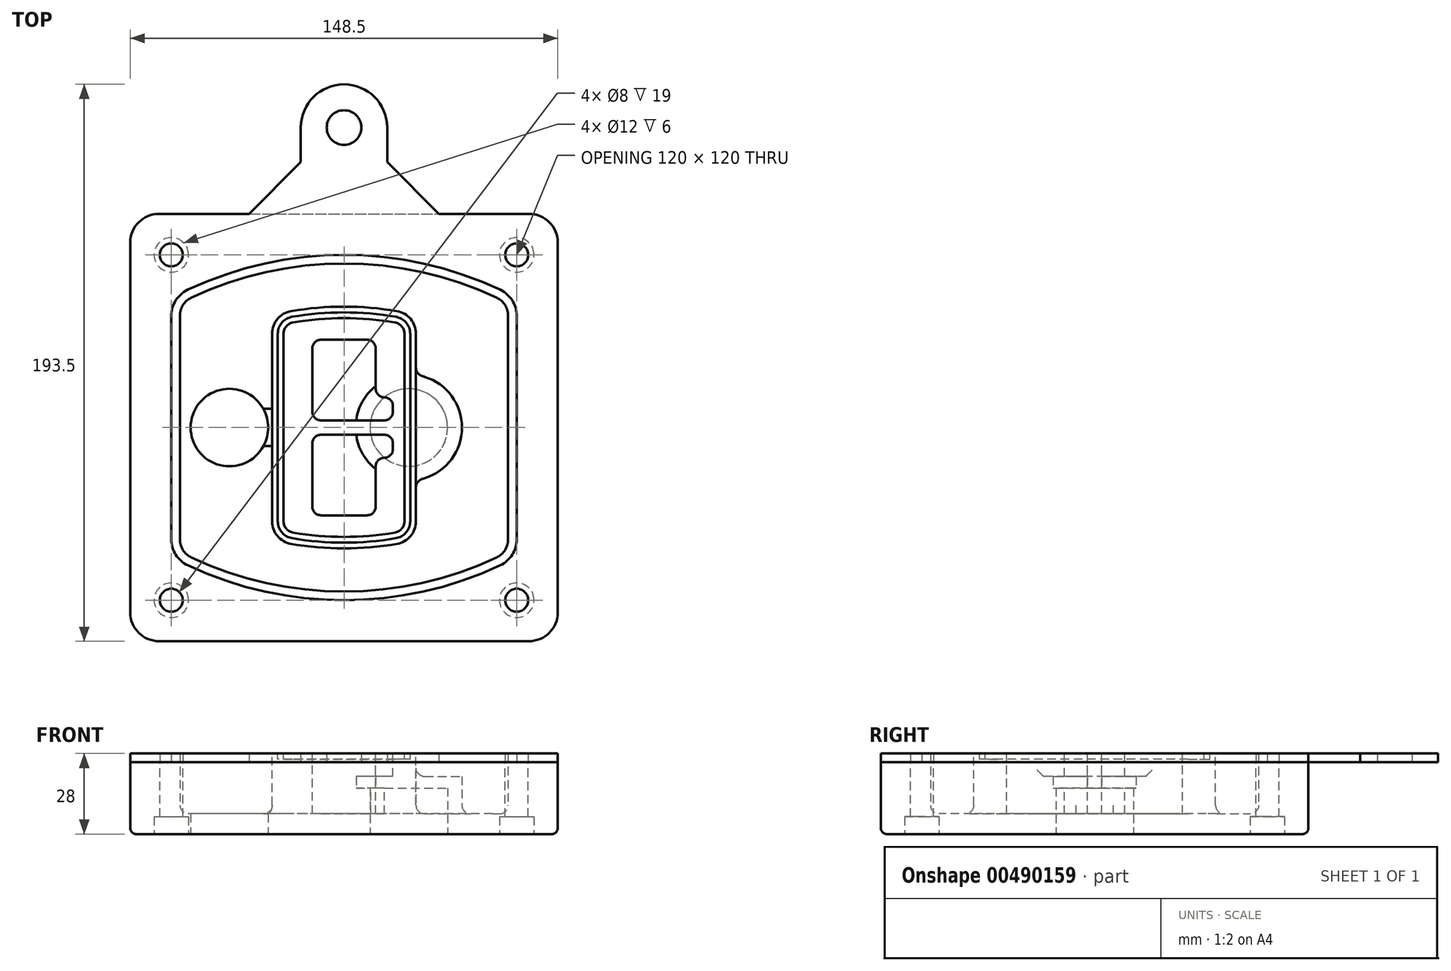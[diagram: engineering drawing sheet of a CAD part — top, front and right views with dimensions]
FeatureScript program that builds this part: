
annotation { "Feature Type Name" : "Feature", "Feature Type Description" : "" }
export const myFeature = defineFeature(function(context is Context, id is Id, definition is map)
    precondition{}
    {
        {
            var Q0;
            Q0=qCreatedBy(makeId("Top.planeOp"),FACE);
            var sketch = newSketch(context, id + "F0", { "sketchPlane" : qUnion([Q0])});
            skPoint(sketch, "E0.rect.middle", {"position": v(0, 0) * mm});
            skLineSegment(sketch, "E1.bottom", {"start": v(-64.25, -74.25) * mm, "end": v(64.25, -74.25) * mm});
            skLineSegment(sketch, "E1.top", {"start": v(-64.25, 74.25) * mm, "end": v(64.25, 74.25) * mm});
            skLineSegment(sketch, "E1.left", {"start": v(-74.25, -64.25) * mm, "end": v(-74.25, 64.25) * mm});
            skLineSegment(sketch, "E1.right", {"start": v(74.25, -64.25) * mm, "end": v(74.25, 64.25) * mm});
            skLineSegment(sketch, "E2", {"start": v(-74.25, 74.25) * mm, "end": v(74.25, -74.25) * mm, "construction": true});
            skLineSegment(sketch, "E3", {"start": v(74.25, 74.25) * mm, "end": v(-74.25, -74.25) * mm, "construction": true});
            skCircle(sketch, "E4", {"center": v(-60, 60) * mm, "radius": 4 * mm});
            skCircle(sketch, "E5", {"center": v(60, 60) * mm, "radius": 4 * mm});
            skCircle(sketch, "E6", {"center": v(60, -60) * mm, "radius": 4 * mm});
            skCircle(sketch, "E7", {"center": v(-60, -60) * mm, "radius": 4 * mm});
            skLineSegment(sketch, "E8", {"start": v(-60, 60) * mm, "end": v(60, 60) * mm, "construction": true});
            skLineSegment(sketch, "E9", {"start": v(60, 60) * mm, "end": v(60, -60) * mm, "construction": true});
            skLineSegment(sketch, "E10", {"start": v(60, -60) * mm, "end": v(-60, -60) * mm, "construction": true});
            skLineSegment(sketch, "E11", {"start": v(-60, -60) * mm, "end": v(-60, 60) * mm, "construction": true});
            skLineSegment(sketch, "E12", {"start": v(-60, 38.83) * mm, "end": v(-60, -38.83) * mm});
            skLineSegment(sketch, "E13", {"start": v(60, 38.83) * mm, "end": v(60, -38.83) * mm});
            skArc(sketch, "E14", {"start": v(54.26, 47.88) * mm, "mid": v(0, 60) * mm, "end": v(-54.26, 47.88) * mm});
            skArc(sketch, "E15", {"start": v(-54.26, -47.88) * mm, "mid": v(0, -60) * mm, "end": v(54.26, -47.88) * mm});
            skLineSegment(sketch, "E16", {"start": v(-60, 0) * mm, "end": v(60, 0) * mm, "construction": true});
            skPoint(sketch, "E17.visualSharp", {"position": v(-60, -45) * mm});
            skArc(sketch, "E17.filletArc", {"start": v(-60, -38.83) * mm, "mid": v(-58.44, -44.2) * mm, "end": v(-54.26, -47.88) * mm});
            skPoint(sketch, "E18.visualSharp", {"position": v(-60, 45) * mm});
            skArc(sketch, "E18.filletArc", {"start": v(-54.26, 47.88) * mm, "mid": v(-58.44, 44.2) * mm, "end": v(-60, 38.83) * mm});
            skPoint(sketch, "E19.visualSharp", {"position": v(60, 45) * mm});
            skArc(sketch, "E19.filletArc", {"start": v(60, 38.83) * mm, "mid": v(58.44, 44.2) * mm, "end": v(54.26, 47.88) * mm});
            skPoint(sketch, "E20.visualSharp", {"position": v(60, -45) * mm});
            skArc(sketch, "E20.filletArc", {"start": v(54.26, -47.88) * mm, "mid": v(58.44, -44.2) * mm, "end": v(60, -38.83) * mm});
            skPoint(sketch, "E21.visualSharp", {"position": v(-74.25, 74.25) * mm});
            skArc(sketch, "E21.filletArc", {"start": v(-64.25, 74.25) * mm, "mid": v(-71.32, 71.32) * mm, "end": v(-74.25, 64.25) * mm});
            skPoint(sketch, "E22.visualSharp", {"position": v(74.25, 74.25) * mm});
            skArc(sketch, "E22.filletArc", {"start": v(74.25, 64.25) * mm, "mid": v(71.32, 71.32) * mm, "end": v(64.25, 74.25) * mm});
            skPoint(sketch, "E23.visualSharp", {"position": v(74.25, -74.25) * mm});
            skArc(sketch, "E23.filletArc", {"start": v(64.25, -74.25) * mm, "mid": v(71.32, -71.32) * mm, "end": v(74.25, -64.25) * mm});
            skPoint(sketch, "E24.visualSharp", {"position": v(-74.25, -74.25) * mm});
            skArc(sketch, "E24.filletArc", {"start": v(-74.25, -64.25) * mm, "mid": v(-71.32, -71.32) * mm, "end": v(-64.25, -74.25) * mm});
            skArc(sketch, "E25.0", {"start": v(57, 38.83) * mm, "mid": v(55.9, 42.58) * mm, "end": v(52.98, 45.17) * mm});
            skLineSegment(sketch, "E25.1", {"start": v(57, 38.83) * mm, "end": v(57, -38.83) * mm});
            skArc(sketch, "E25.2", {"start": v(52.98, -45.17) * mm, "mid": v(55.9, -42.58) * mm, "end": v(57, -38.83) * mm});
            skArc(sketch, "E25.3", {"start": v(-52.98, -45.17) * mm, "mid": v(0, -57) * mm, "end": v(52.98, -45.17) * mm});
            skArc(sketch, "E25.4", {"start": v(-57, -38.83) * mm, "mid": v(-55.9, -42.58) * mm, "end": v(-52.98, -45.17) * mm});
            skArc(sketch, "E25.5", {"start": v(52.98, 45.17) * mm, "mid": v(0, 57) * mm, "end": v(-52.98, 45.17) * mm});
            skLineSegment(sketch, "E25.6", {"start": v(-57, 38.83) * mm, "end": v(-57, -38.83) * mm});
            skArc(sketch, "E25.7", {"start": v(-52.98, 45.17) * mm, "mid": v(-55.9, 42.58) * mm, "end": v(-57, 38.83) * mm});
            skArc(sketch, "E26.0", {"start": v(-55.96, 51.5) * mm, "mid": v(-61.82, 46.33) * mm, "end": v(-64, 38.83) * mm});
            skArc(sketch, "E26.1", {"start": v(55.96, 51.5) * mm, "mid": v(0, 64) * mm, "end": v(-55.96, 51.5) * mm});
            skArc(sketch, "E26.2", {"start": v(64, 38.83) * mm, "mid": v(61.82, 46.33) * mm, "end": v(55.96, 51.5) * mm});
            skLineSegment(sketch, "E26.3", {"start": v(64, 38.83) * mm, "end": v(64, -38.83) * mm});
            skArc(sketch, "E26.4", {"start": v(55.96, -51.5) * mm, "mid": v(61.82, -46.33) * mm, "end": v(64, -38.83) * mm});
            skLineSegment(sketch, "E26.5", {"start": v(-64, 38.83) * mm, "end": v(-64, -38.83) * mm});
            skArc(sketch, "E26.6", {"start": v(-55.96, -51.5) * mm, "mid": v(0, -64) * mm, "end": v(55.96, -51.5) * mm});
            skArc(sketch, "E26.7", {"start": v(-64, -38.83) * mm, "mid": v(-61.82, -46.33) * mm, "end": v(-55.96, -51.5) * mm});
            skSolve(sketch);
        }
        {
            var Q0;
            Q0=makeQuery(id+"F0.imprint","IMPRINT",FACE,{"disambiguationData":[TD([[makeQuery(id+"F0.imprint","IMPRINT",EDGE,{"derivedFrom":sQuery(id+"F0.wireOp",EDGE,"E1.bottom")}),1.0]])]});
            var Q1;
            Q1=makeQuery(id+"F0.imprint","IMPRINT",FACE,{"disambiguationData":[TD([[makeQuery(id+"F0.imprint","IMPRINT",EDGE,{"derivedFrom":sQuery(id+"F0.wireOp",EDGE,"E12")}),1.0]])]});
            var Q2;
            Q2=makeQuery(id+"F0.imprint","IMPRINT",FACE,{"disambiguationData":[TD([[makeQuery(id+"F0.imprint","IMPRINT",EDGE,{"derivedFrom":sQuery(id+"F0.wireOp",EDGE,"E25.0")}),1.0]])]});
            var Q3;
            Q3=makeQuery(id+"F0.imprint","IMPRINT",FACE,{"disambiguationData":[TD([[makeQuery(id+"F0.imprint","IMPRINT",EDGE,{"derivedFrom":sQuery(id+"F0.wireOp",EDGE,"E12")}),-1.0]])]});
            extrude(context, id + "F1", {"entities" : qUnion([Q0, Q1, Q2, Q3]), "oppositeDirection" : true, "depth" : 25 * mm});
        }
        {
            var Q0;
            Q0=makeQuery(id+"F0.imprint","IMPRINT",FACE,{"disambiguationData":[TD([[makeQuery(id+"F0.imprint","IMPRINT",EDGE,{"derivedFrom":sQuery(id+"F0.wireOp",EDGE,"E12")}),1.0]])]});
            extrude(context, id + "F2", {"entities" : qUnion([Q0]), "operationType" : NewBodyOperationType.ADD, "depth" : 3 * mm});
        }
        {
            var Q0;
            Q0=makeQuery(id+"F0.imprint","IMPRINT",FACE,{"disambiguationData":[TD([[makeQuery(id+"F0.imprint","IMPRINT",EDGE,{"derivedFrom":sQuery(id+"F0.wireOp",EDGE,"E25.0")}),1.0]])]});
            extrude(context, id + "F3", {"entities" : qUnion([Q0]), "operationType" : NewBodyOperationType.REMOVE, "oppositeDirection" : true, "depth" : 18 * mm});
        }
        {
            var Q0;
            Q0=makeQuery(id+"F2.opExtrude","CAP_FACE",FACE,{"disambiguationData":[OSD([sQuery(id+"F0.wireOp",EDGE,"E12"),sQuery(id+"F0.wireOp",EDGE,"E13"),sQuery(id+"F0.wireOp",EDGE,"E14"),sQuery(id+"F0.wireOp",EDGE,"E15"),sQuery(id+"F0.wireOp",EDGE,"E17.filletArc"),sQuery(id+"F0.wireOp",EDGE,"E18.filletArc"),sQuery(id+"F0.wireOp",EDGE,"E19.filletArc"),sQuery(id+"F0.wireOp",EDGE,"E20.filletArc"),sQuery(id+"F0.wireOp",EDGE,"E25.0"),sQuery(id+"F0.wireOp",EDGE,"E25.1"),sQuery(id+"F0.wireOp",EDGE,"E25.2"),sQuery(id+"F0.wireOp",EDGE,"E25.3"),sQuery(id+"F0.wireOp",EDGE,"E25.4"),sQuery(id+"F0.wireOp",EDGE,"E25.5"),sQuery(id+"F0.wireOp",EDGE,"E25.6"),sQuery(id+"F0.wireOp",EDGE,"E25.7")])],"isStart":false});
            var sketch = newSketch(context, id + "F4", { "sketchPlane" : qUnion([Q0])});
            skArc(sketch, "E27.0", {"start": v(-18.34, -40.45) * mm, "mid": v(0, -42) * mm, "end": v(18.34, -40.45) * mm});
            skArc(sketch, "E28.0", {"start": v(18.34, 40.45) * mm, "mid": v(0, 42) * mm, "end": v(-18.34, 40.45) * mm});
            skLineSegment(sketch, "E29", {"start": v(-25, 32.57) * mm, "end": v(-25, -32.57) * mm});
            skLineSegment(sketch, "E30", {"start": v(25, 32.57) * mm, "end": v(25, -32.57) * mm});
            skLineSegment(sketch, "E31", {"start": v(-25, 39.1) * mm, "end": v(25, 39.1) * mm, "construction": true});
            skLineSegment(sketch, "E32", {"start": v(-25, -39.1) * mm, "end": v(25, -39.1) * mm, "construction": true});
            skPoint(sketch, "E33.visualSharp", {"position": v(-25, 39.1) * mm});
            skArc(sketch, "E33.filletArc", {"start": v(-18.34, 40.45) * mm, "mid": v(-23.11, 37.73) * mm, "end": v(-25, 32.57) * mm});
            skPoint(sketch, "E34.visualSharp", {"position": v(25, 39.1) * mm});
            skArc(sketch, "E34.filletArc", {"start": v(25, 32.57) * mm, "mid": v(23.11, 37.73) * mm, "end": v(18.34, 40.45) * mm});
            skPoint(sketch, "E35.visualSharp", {"position": v(25, -39.1) * mm});
            skArc(sketch, "E35.filletArc", {"start": v(18.34, -40.45) * mm, "mid": v(23.11, -37.73) * mm, "end": v(25, -32.57) * mm});
            skPoint(sketch, "E36.visualSharp", {"position": v(-25, -39.1) * mm});
            skArc(sketch, "E36.filletArc", {"start": v(-25, -32.57) * mm, "mid": v(-23.11, -37.73) * mm, "end": v(-18.34, -40.45) * mm});
            skArc(sketch, "E37.0", {"start": v(52.98, 45.17) * mm, "mid": v(0, 57) * mm, "end": v(-52.98, 45.17) * mm});
            skArc(sketch, "E37.1", {"start": v(-52.98, 45.17) * mm, "mid": v(-55.9, 42.58) * mm, "end": v(-57, 38.83) * mm});
            skLineSegment(sketch, "E37.2", {"start": v(-57, 38.83) * mm, "end": v(-57, -38.83) * mm});
            skArc(sketch, "E37.3", {"start": v(-57, -38.83) * mm, "mid": v(-55.9, -42.58) * mm, "end": v(-52.98, -45.17) * mm});
            skArc(sketch, "E37.4", {"start": v(-52.98, -45.17) * mm, "mid": v(0, -57) * mm, "end": v(52.98, -45.17) * mm});
            skArc(sketch, "E37.5", {"start": v(52.98, -45.17) * mm, "mid": v(55.9, -42.58) * mm, "end": v(57, -38.83) * mm});
            skLineSegment(sketch, "E37.6", {"start": v(57, 38.83) * mm, "end": v(57, -38.83) * mm});
            skArc(sketch, "E37.7", {"start": v(57, 38.83) * mm, "mid": v(55.9, 42.58) * mm, "end": v(52.98, 45.17) * mm});
            skLineSegment(sketch, "E38.0", {"start": v(23, 32.57) * mm, "end": v(23, -32.57) * mm});
            skArc(sketch, "E38.1", {"start": v(18, -38.48) * mm, "mid": v(21.58, -36.44) * mm, "end": v(23, -32.57) * mm});
            skArc(sketch, "E38.2", {"start": v(-18, -38.48) * mm, "mid": v(0, -40) * mm, "end": v(18, -38.48) * mm});
            skArc(sketch, "E38.3", {"start": v(-23, -32.57) * mm, "mid": v(-21.58, -36.44) * mm, "end": v(-18, -38.48) * mm});
            skLineSegment(sketch, "E38.4", {"start": v(-23, 32.57) * mm, "end": v(-23, -32.57) * mm});
            skArc(sketch, "E38.5", {"start": v(23, 32.57) * mm, "mid": v(21.58, 36.44) * mm, "end": v(18, 38.48) * mm});
            skArc(sketch, "E38.6", {"start": v(-18, 38.48) * mm, "mid": v(-21.58, 36.44) * mm, "end": v(-23, 32.57) * mm});
            skArc(sketch, "E38.7", {"start": v(18, 38.48) * mm, "mid": v(0, 40) * mm, "end": v(-18, 38.48) * mm});
            skArc(sketch, "E39.0", {"start": v(21, 32.57) * mm, "mid": v(20.06, 35.15) * mm, "end": v(17.67, 36.5) * mm});
            skLineSegment(sketch, "E39.1", {"start": v(21, 32.57) * mm, "end": v(21, -32.57) * mm});
            skArc(sketch, "E39.2", {"start": v(17.67, -36.5) * mm, "mid": v(20.06, -35.15) * mm, "end": v(21, -32.57) * mm});
            skArc(sketch, "E39.3", {"start": v(-17.67, -36.5) * mm, "mid": v(0, -38) * mm, "end": v(17.67, -36.5) * mm});
            skArc(sketch, "E39.4", {"start": v(-21, -32.57) * mm, "mid": v(-20.06, -35.15) * mm, "end": v(-17.67, -36.5) * mm});
            skArc(sketch, "E39.5", {"start": v(17.67, 36.5) * mm, "mid": v(0, 38) * mm, "end": v(-17.67, 36.5) * mm});
            skLineSegment(sketch, "E39.6", {"start": v(-21, 32.57) * mm, "end": v(-21, -32.57) * mm});
            skArc(sketch, "E39.7", {"start": v(-17.67, 36.5) * mm, "mid": v(-20.06, 35.15) * mm, "end": v(-21, 32.57) * mm});
            skLineSegment(sketch, "E40", {"start": v(-25, 0) * mm, "end": v(25, 0) * mm, "construction": true});
            skLineSegment(sketch, "E41", {"start": v(-11, 5.5) * mm, "end": v(-11, 27.5) * mm});
            skLineSegment(sketch, "E42", {"start": v(-8, 30.5) * mm, "end": v(8, 30.5) * mm});
            skLineSegment(sketch, "E43", {"start": v(11, 27.5) * mm, "end": v(11, 13.5) * mm});
            skLineSegment(sketch, "E44", {"start": v(14, 10.5) * mm, "end": v(14, 10.5) * mm});
            skLineSegment(sketch, "E45", {"start": v(17, 7.5) * mm, "end": v(17, 5.5) * mm});
            skLineSegment(sketch, "E46", {"start": v(14, 2.5) * mm, "end": v(-8, 2.5) * mm});
            skPoint(sketch, "E47.visualSharp", {"position": v(-11, 30.5) * mm});
            skArc(sketch, "E47.filletArc", {"start": v(-8, 30.5) * mm, "mid": v(-10.12, 29.62) * mm, "end": v(-11, 27.5) * mm});
            skPoint(sketch, "E48.visualSharp", {"position": v(11, 30.5) * mm});
            skArc(sketch, "E48.filletArc", {"start": v(11, 27.5) * mm, "mid": v(10.12, 29.62) * mm, "end": v(8, 30.5) * mm});
            skPoint(sketch, "E49.visualSharp", {"position": v(11, 10.5) * mm});
            skArc(sketch, "E49.filletArc", {"start": v(11, 13.5) * mm, "mid": v(11.88, 11.38) * mm, "end": v(14, 10.5) * mm});
            skPoint(sketch, "E50.visualSharp", {"position": v(17, 10.5) * mm});
            skArc(sketch, "E50.filletArc", {"start": v(17, 7.5) * mm, "mid": v(16.12, 9.62) * mm, "end": v(14, 10.5) * mm});
            skPoint(sketch, "E51.visualSharp", {"position": v(17, 2.5) * mm});
            skArc(sketch, "E51.filletArc", {"start": v(14, 2.5) * mm, "mid": v(16.12, 3.38) * mm, "end": v(17, 5.5) * mm});
            skPoint(sketch, "E52.visualSharp", {"position": v(-11, 2.5) * mm});
            skArc(sketch, "E52.filletArc", {"start": v(-11, 5.5) * mm, "mid": v(-10.12, 3.38) * mm, "end": v(-8, 2.5) * mm});
            skLineSegment(sketch, "E53.0.MirrorCS", {"start": v(14, -2.5) * mm, "end": v(-8, -2.5) * mm});
            skArc(sketch, "E54.0.MirrorCS", {"start": v(-11, -5.5) * mm, "mid": v(-10.12, -3.38) * mm, "end": v(-8, -2.5) * mm});
            skLineSegment(sketch, "E55.0.MirrorCS", {"start": v(-11, -5.5) * mm, "end": v(-11, -27.5) * mm});
            skArc(sketch, "E56.0.MirrorCS", {"start": v(-8, -30.5) * mm, "mid": v(-10.12, -29.62) * mm, "end": v(-11, -27.5) * mm});
            skLineSegment(sketch, "E57.0.MirrorCS", {"start": v(-8, -30.5) * mm, "end": v(8, -30.5) * mm});
            skArc(sketch, "E58.0.MirrorCS", {"start": v(11, -27.5) * mm, "mid": v(10.12, -29.62) * mm, "end": v(8, -30.5) * mm});
            skLineSegment(sketch, "E59.0.MirrorCS", {"start": v(11, -27.5) * mm, "end": v(11, -13.5) * mm});
            skArc(sketch, "E60.0.MirrorCS", {"start": v(11, -13.5) * mm, "mid": v(11.88, -11.38) * mm, "end": v(14, -10.5) * mm});
            skArc(sketch, "E61.0.MirrorCS", {"start": v(17, -7.5) * mm, "mid": v(16.12, -9.62) * mm, "end": v(14, -10.5) * mm});
            skLineSegment(sketch, "E62.0.MirrorCS", {"start": v(17, -7.5) * mm, "end": v(17, -5.5) * mm});
            skArc(sketch, "E63.0.MirrorCS", {"start": v(14, -2.5) * mm, "mid": v(16.12, -3.38) * mm, "end": v(17, -5.5) * mm});
            skSolve(sketch);
        }
        {
            var Q0;
            Q0=makeQuery(id+"F4.imprint","IMPRINT",FACE,{"disambiguationData":[TD([[makeQuery(id+"F4.imprint","IMPRINT",EDGE,{"derivedFrom":sQuery(id+"F4.wireOp",EDGE,"E27.0")}),1.0]])]});
            var Q1;
            Q1=makeQuery(id+"F4.imprint","IMPRINT",FACE,{"disambiguationData":[TD([[makeQuery(id+"F4.imprint","IMPRINT",EDGE,{"derivedFrom":sQuery(id+"F4.wireOp",EDGE,"E38.0")}),-1.0]])]});
            var Q2;
            Q2=makeQuery(id+"F4.imprint","IMPRINT",FACE,{"disambiguationData":[TD([[makeQuery(id+"F4.imprint","IMPRINT",EDGE,{"derivedFrom":sQuery(id+"F4.wireOp",EDGE,"E39.0")}),1.0]])]});
            extrude(context, id + "F5", {"entities" : qUnion([Q0, Q1, Q2]), "operationType" : NewBodyOperationType.ADD, "endBound" : BoundingType.UP_TO_NEXT, "oppositeDirection" : true, "depth" : 25 * mm});
        }
        {
            var Q0;
            Q0=makeQuery(id+"F4.imprint","IMPRINT",FACE,{"disambiguationData":[TD([[makeQuery(id+"F4.imprint","IMPRINT",EDGE,{"derivedFrom":sQuery(id+"F4.wireOp",EDGE,"E38.0")}),-1.0]])]});
            extrude(context, id + "F6", {"entities" : qUnion([Q0]), "operationType" : NewBodyOperationType.REMOVE, "oppositeDirection" : true, "depth" : 2 * mm});
        }
        {
            var Q0;
            Q0=makeQuery(id+"F1.opExtrude","CAP_FACE",FACE,{"disambiguationData":[OSD([sQuery(id+"F0.wireOp",EDGE,"E1.bottom"),sQuery(id+"F0.wireOp",EDGE,"E1.top"),sQuery(id+"F0.wireOp",EDGE,"E1.left"),sQuery(id+"F0.wireOp",EDGE,"E1.right"),sQuery(id+"F0.wireOp",EDGE,"E4"),sQuery(id+"F0.wireOp",EDGE,"E5"),sQuery(id+"F0.wireOp",EDGE,"E6"),sQuery(id+"F0.wireOp",EDGE,"E7"),sQuery(id+"F0.wireOp",EDGE,"E21.filletArc"),sQuery(id+"F0.wireOp",EDGE,"E22.filletArc"),sQuery(id+"F0.wireOp",EDGE,"E23.filletArc"),sQuery(id+"F0.wireOp",EDGE,"E24.filletArc")])],"isStart":false});
            var sketch = newSketch(context, id + "F7", { "sketchPlane" : qUnion([Q0])});
            skCircle(sketch, "E64", {"center": v(22.5, 0) * mm, "radius": 13.47 * mm});
            skCircle(sketch, "E65", {"center": v(-39.81, 0) * mm, "radius": 13.47 * mm});
            skLineSegment(sketch, "E66", {"start": v(74.25, 0) * mm, "end": v(-74.25, 0) * mm});
            skCircle(sketch, "E67", {"center": v(22.5, 0) * mm, "radius": 18.47 * mm});
            skCircle(sketch, "E68", {"center": v(60, -60) * mm, "radius": 6 * mm});
            skCircle(sketch, "E69", {"center": v(-60, -60) * mm, "radius": 6 * mm});
            skCircle(sketch, "E70", {"center": v(-60, 60) * mm, "radius": 6 * mm});
            skCircle(sketch, "E71", {"center": v(60, 60) * mm, "radius": 6 * mm});
            skSolve(sketch);
        }
        {
            var Q0;
            {var subQ1=sQuery(id+"F7.wireOp",EDGE,"E66");var subQ4=sQuery(id+"F7.wireOp",EDGE,"E64");var subQ6=makeQuery(id+"F7.imprint","INTERSECT",VERTEX,{"disambiguationData":[OD(0.0)],"derivedFrom":[subQ4,subQ1]});Q0=makeQuery(id+"F7.imprint","IMPRINT",FACE,{"disambiguationData":[TD([[makeQuery(id+"F7.imprint","IMPRINT",EDGE,{"disambiguationData":[TD([[subQ6,-1.0]])],"derivedFrom":subQ4}),-1.0]])]});}
            var Q1;
            {var subQ0=sQuery(id+"F7.wireOp",EDGE,"E66");var subQ1=sQuery(id+"F7.wireOp",EDGE,"E64");var subQ3=makeQuery(id+"F7.imprint","INTERSECT",VERTEX,{"disambiguationData":[OD(0.0)],"derivedFrom":[subQ1,subQ0]});Q1=makeQuery(id+"F7.imprint","IMPRINT",FACE,{"disambiguationData":[TD([[makeQuery(id+"F7.imprint","IMPRINT",EDGE,{"disambiguationData":[TD([[subQ3,-1.0]])],"derivedFrom":subQ1}),1.0]])]});}
            var Q2;
            {var subQ0=sQuery(id+"F7.wireOp",EDGE,"E66");var subQ1=sQuery(id+"F7.wireOp",EDGE,"E64");var subQ3=makeQuery(id+"F7.imprint","INTERSECT",VERTEX,{"disambiguationData":[OD(0.0)],"derivedFrom":[subQ1,subQ0]});Q2=makeQuery(id+"F7.imprint","IMPRINT",FACE,{"disambiguationData":[TD([[makeQuery(id+"F7.imprint","IMPRINT",EDGE,{"disambiguationData":[TD([[subQ3,1.0]])],"derivedFrom":subQ1}),1.0]])]});}
            var Q3;
            {var subQ1=sQuery(id+"F7.wireOp",EDGE,"E66");var subQ4=sQuery(id+"F7.wireOp",EDGE,"E64");var subQ6=makeQuery(id+"F7.imprint","INTERSECT",VERTEX,{"disambiguationData":[OD(0.0)],"derivedFrom":[subQ4,subQ1]});Q3=makeQuery(id+"F7.imprint","IMPRINT",FACE,{"disambiguationData":[TD([[makeQuery(id+"F7.imprint","IMPRINT",EDGE,{"disambiguationData":[TD([[subQ6,1.0]])],"derivedFrom":subQ4}),-1.0]])]});}
            extrude(context, id + "F8", {"entities" : qUnion([Q0, Q1, Q2, Q3]), "operationType" : NewBodyOperationType.ADD, "oppositeDirection" : true, "depth" : 20 * mm});
        }
        {
            var Q0;
            {var subQ0=sQuery(id+"F7.wireOp",EDGE,"E66");var subQ1=sQuery(id+"F7.wireOp",EDGE,"E64");var subQ3=makeQuery(id+"F7.imprint","INTERSECT",VERTEX,{"disambiguationData":[OD(0.0)],"derivedFrom":[subQ1,subQ0]});Q0=makeQuery(id+"F7.imprint","IMPRINT",FACE,{"disambiguationData":[TD([[makeQuery(id+"F7.imprint","IMPRINT",EDGE,{"disambiguationData":[TD([[subQ3,-1.0]])],"derivedFrom":subQ1}),1.0]])]});}
            var Q1;
            {var subQ0=sQuery(id+"F7.wireOp",EDGE,"E66");var subQ1=sQuery(id+"F7.wireOp",EDGE,"E64");var subQ3=makeQuery(id+"F7.imprint","INTERSECT",VERTEX,{"disambiguationData":[OD(0.0)],"derivedFrom":[subQ1,subQ0]});Q1=makeQuery(id+"F7.imprint","IMPRINT",FACE,{"disambiguationData":[TD([[makeQuery(id+"F7.imprint","IMPRINT",EDGE,{"disambiguationData":[TD([[subQ3,1.0]])],"derivedFrom":subQ1}),1.0]])]});}
            extrude(context, id + "F9", {"entities" : qUnion([Q0, Q1]), "operationType" : NewBodyOperationType.REMOVE, "oppositeDirection" : true, "depth" : 16 * mm});
        }
        {
            var Q0;
            {var subQ0=sQuery(id+"F7.wireOp",EDGE,"E66");var subQ1=sQuery(id+"F7.wireOp",EDGE,"E65");var subQ3=makeQuery(id+"F7.imprint","INTERSECT",VERTEX,{"disambiguationData":[OD(0.0)],"derivedFrom":[subQ1,subQ0]});Q0=makeQuery(id+"F7.imprint","IMPRINT",FACE,{"disambiguationData":[TD([[makeQuery(id+"F7.imprint","IMPRINT",EDGE,{"disambiguationData":[TD([[subQ3,-1.0]])],"derivedFrom":subQ1}),1.0]])]});}
            var Q1;
            {var subQ0=sQuery(id+"F7.wireOp",EDGE,"E66");var subQ1=sQuery(id+"F7.wireOp",EDGE,"E65");var subQ3=makeQuery(id+"F7.imprint","INTERSECT",VERTEX,{"disambiguationData":[OD(0.0)],"derivedFrom":[subQ1,subQ0]});Q1=makeQuery(id+"F7.imprint","IMPRINT",FACE,{"disambiguationData":[TD([[makeQuery(id+"F7.imprint","IMPRINT",EDGE,{"disambiguationData":[TD([[subQ3,1.0]])],"derivedFrom":subQ1}),1.0]])]});}
            extrude(context, id + "F10", {"entities" : qUnion([Q0, Q1]), "operationType" : NewBodyOperationType.REMOVE, "oppositeDirection" : true, "depth" : 25 * mm});
        }
        {
            var Q0;
            Q0=makeQuery(id+"F7.imprint","IMPRINT",FACE,{"disambiguationData":[TD([[makeQuery(id+"F7.imprint","IMPRINT",EDGE,{"derivedFrom":sQuery(id+"F7.wireOp",EDGE,"E68")}),1.0]])]});
            var Q1;
            Q1=makeQuery(id+"F7.imprint","IMPRINT",FACE,{"disambiguationData":[TD([[makeQuery(id+"F7.imprint","IMPRINT",EDGE,{"derivedFrom":makeQuery(id+"F1.opExtrude","CAP_EDGE",EDGE,{"disambiguationData":[OSD([sQuery(id+"F0.wireOp",EDGE,"E5")])],"isStart":false})}),-1.0]])]});
            var Q2;
            Q2=makeQuery(id+"F7.imprint","IMPRINT",FACE,{"disambiguationData":[TD([[makeQuery(id+"F7.imprint","IMPRINT",EDGE,{"derivedFrom":sQuery(id+"F7.wireOp",EDGE,"E69")}),1.0]])]});
            var Q3;
            Q3=makeQuery(id+"F7.imprint","IMPRINT",FACE,{"disambiguationData":[TD([[makeQuery(id+"F7.imprint","IMPRINT",EDGE,{"derivedFrom":makeQuery(id+"F1.opExtrude","CAP_EDGE",EDGE,{"disambiguationData":[OSD([sQuery(id+"F0.wireOp",EDGE,"E4")])],"isStart":false})}),-1.0]])]});
            var Q4;
            Q4=makeQuery(id+"F7.imprint","IMPRINT",FACE,{"disambiguationData":[TD([[makeQuery(id+"F7.imprint","IMPRINT",EDGE,{"derivedFrom":sQuery(id+"F7.wireOp",EDGE,"E70")}),1.0]])]});
            var Q5;
            Q5=makeQuery(id+"F7.imprint","IMPRINT",FACE,{"disambiguationData":[TD([[makeQuery(id+"F7.imprint","IMPRINT",EDGE,{"derivedFrom":makeQuery(id+"F1.opExtrude","CAP_EDGE",EDGE,{"disambiguationData":[OSD([sQuery(id+"F0.wireOp",EDGE,"E7")])],"isStart":false})}),-1.0]])]});
            var Q6;
            Q6=makeQuery(id+"F7.imprint","IMPRINT",FACE,{"disambiguationData":[TD([[makeQuery(id+"F7.imprint","IMPRINT",EDGE,{"derivedFrom":sQuery(id+"F7.wireOp",EDGE,"E71")}),1.0]])]});
            var Q7;
            Q7=makeQuery(id+"F7.imprint","IMPRINT",FACE,{"disambiguationData":[TD([[makeQuery(id+"F7.imprint","IMPRINT",EDGE,{"derivedFrom":makeQuery(id+"F1.opExtrude","CAP_EDGE",EDGE,{"disambiguationData":[OSD([sQuery(id+"F0.wireOp",EDGE,"E6")])],"isStart":false})}),-1.0]])]});
            extrude(context, id + "F11", {"entities" : qUnion([Q0, Q1, Q2, Q3, Q4, Q5, Q6, Q7]), "operationType" : NewBodyOperationType.REMOVE, "oppositeDirection" : true, "depth" : 6 * mm});
        }
        {
            var Q0;
            Q0=makeQuery(id+"F9.boolean.opBoolean","COPY",FACE,{"derivedFrom":makeQuery(id+"F9.opExtrude","CAP_FACE",FACE,{"disambiguationData":[OSD([sQuery(id+"F7.wireOp",EDGE,"E64")])],"isStart":false})});
            var sketch = newSketch(context, id + "F12", { "sketchPlane" : qUnion([Q0])});
            skArc(sketch, "E72.0", {"start": v(11, 14.45) * mm, "mid": v(6.45, 9.13) * mm, "end": v(4.2, 2.5) * mm});
            skArc(sketch, "E72.1", {"start": v(4.2, -2.5) * mm, "mid": v(6.45, -9.13) * mm, "end": v(11, -14.45) * mm});
            skLineSegment(sketch, "E73", {"start": v(4.2, -2.5) * mm, "end": v(14, -2.5) * mm});
            skLineSegment(sketch, "E74.0", {"start": v(14, 2.5) * mm, "end": v(4.2, 2.5) * mm});
            skArc(sketch, "E74.1", {"start": v(14, 2.5) * mm, "mid": v(16.12, 3.38) * mm, "end": v(17, 5.5) * mm});
            skLineSegment(sketch, "E74.2", {"start": v(17, 7.5) * mm, "end": v(17, 5.5) * mm});
            skArc(sketch, "E74.3", {"start": v(17, 7.5) * mm, "mid": v(16.12, 9.62) * mm, "end": v(14, 10.5) * mm});
            skArc(sketch, "E74.4", {"start": v(11, 13.5) * mm, "mid": v(11.88, 11.38) * mm, "end": v(14, 10.5) * mm});
            skLineSegment(sketch, "E74.5", {"start": v(11, 14.45) * mm, "end": v(11, 13.5) * mm});
            skLineSegment(sketch, "E74.7", {"start": v(14, -2.5) * mm, "end": v(4.2, -2.5) * mm});
            skArc(sketch, "E74.8", {"start": v(14, -2.5) * mm, "mid": v(16.12, -3.38) * mm, "end": v(17, -5.5) * mm});
            skLineSegment(sketch, "E74.9", {"start": v(17, -7.5) * mm, "end": v(17, -5.5) * mm});
            skArc(sketch, "E74.10", {"start": v(17, -7.5) * mm, "mid": v(16.12, -9.62) * mm, "end": v(14, -10.5) * mm});
            skArc(sketch, "E74.11", {"start": v(11, -13.5) * mm, "mid": v(11.88, -11.38) * mm, "end": v(14, -10.5) * mm});
            skLineSegment(sketch, "E74.12", {"start": v(11, -14.45) * mm, "end": v(11, -13.5) * mm});
            skPoint(sketch, "E75.orphan", {"position": v(11, -27.5) * mm});
            skPoint(sketch, "E76.orphan", {"position": v(-8, -2.5) * mm});
            skPoint(sketch, "E77.orphan", {"position": v(-8, 2.5) * mm});
            skPoint(sketch, "E78.orphan", {"position": v(11, 27.5) * mm});
            skSolve(sketch);
        }
        {
            var Q0;
            {var subQ7=sQuery(id+"F12.wireOp",EDGE,"E72.0");var subQ14=sQuery(id+"F12.wireOp",EDGE,"E72.1");var subQ16=sQuery(id+"F12.wireOp",EDGE,"E74.1");var subQ18=sQuery(id+"F12.wireOp",EDGE,"E74.8");Q0=qUnion([makeQuery(id+"F12.imprint","IMPRINT",FACE,{"disambiguationData":[TD([[makeQuery(id+"F12.imprint","IMPRINT",EDGE,{"derivedFrom":subQ7}),1.0]])]}),makeQuery(id+"F12.imprint","IMPRINT",FACE,{"disambiguationData":[TD([[makeQuery(id+"F12.imprint","IMPRINT",EDGE,{"derivedFrom":subQ14}),1.0]])]}),makeQuery(id+"F12.imprint","IMPRINT",FACE,{"disambiguationData":[TD([[makeQuery(id+"F12.imprint","IMPRINT",EDGE,{"derivedFrom":subQ16}),1.0]])]}),makeQuery(id+"F12.imprint","IMPRINT",FACE,{"disambiguationData":[TD([[makeQuery(id+"F12.imprint","IMPRINT",EDGE,{"derivedFrom":subQ18}),-1.0]])]})]);}
            var Q1;
            Q1=makeQuery(id+"F5.boolean.opBoolean","SPLIT",FACE,{"disambiguationData":[TD([makeQuery(id+"F5.opExtrude","SWEPT_FACE",FACE,{"disambiguationData":[OSD([sQuery(id+"F4.wireOp",EDGE,"E41")])]})])],"derivedFrom":makeQuery(id+"F3.boolean.opBoolean","COPY",FACE,{"derivedFrom":makeQuery(id+"F3.opExtrude","CAP_FACE",FACE,{"disambiguationData":[OSD([sQuery(id+"F0.wireOp",EDGE,"E25.0"),sQuery(id+"F0.wireOp",EDGE,"E25.1"),sQuery(id+"F0.wireOp",EDGE,"E25.2"),sQuery(id+"F0.wireOp",EDGE,"E25.3"),sQuery(id+"F0.wireOp",EDGE,"E25.4"),sQuery(id+"F0.wireOp",EDGE,"E25.5"),sQuery(id+"F0.wireOp",EDGE,"E25.6"),sQuery(id+"F0.wireOp",EDGE,"E25.7")])],"isStart":false})})});
            extrude(context, id + "F13", {"entities" : qUnion([Q0]), "operationType" : NewBodyOperationType.REMOVE, "endBound" : BoundingType.UP_TO_SURFACE, "endBoundEntityFace" : qUnion([Q1]), "depth" : 25 * mm});
        }
        {
            var Q0;
            Q0=makeQuery(id+"F3.boolean.opBoolean","COPY",EDGE,{"derivedFrom":makeQuery(id+"F3.opExtrude","CAP_EDGE",EDGE,{"disambiguationData":[OSD([sQuery(id+"F0.wireOp",EDGE,"E25.6")])],"isStart":false})});
            var Q1;
            Q1=makeQuery(id+"F8.boolean.opBoolean","INTERSECT",EDGE,{"derivedFrom":[makeQuery(id+"F5.opExtrude","SWEPT_FACE",FACE,{"disambiguationData":[OSD([sQuery(id+"F4.wireOp",EDGE,"E30")])]}),makeQuery(id+"F8.opExtrude","CAP_FACE",FACE,{"disambiguationData":[OSD([sQuery(id+"F7.wireOp",EDGE,"E67")])],"isStart":false})]});
            var Q2;
            Q2=makeQuery(id+"F8.boolean.opBoolean","INTERSECT",EDGE,{"disambiguationData":[OD(1.0)],"derivedFrom":[makeQuery(id+"F5.opExtrude","SWEPT_FACE",FACE,{"disambiguationData":[OSD([sQuery(id+"F4.wireOp",EDGE,"E30")])]}),makeQuery(id+"F8.opExtrude","SWEPT_FACE",FACE,{"disambiguationData":[OSD([sQuery(id+"F7.wireOp",EDGE,"E67")])]})]});
            var Q3;
            {var subQ0=sQuery(id+"F4.wireOp",EDGE,"E30");Q3=makeQuery(id+"F8.boolean.opBoolean","SPLIT",EDGE,{"disambiguationData":[TD([makeQuery(id+"F5.opExtrude","SWEPT_FACE",FACE,{"disambiguationData":[OSD([sQuery(id+"F4.wireOp",EDGE,"E35.filletArc")])]})])],"derivedFrom":makeQuery(id+"F5.opExtrude","CAP_EDGE",EDGE,{"disambiguationData":[OSD([subQ0])],"isStart":false})});}
            var Q4;
            {var subQ0=sQuery(id+"F0.wireOp",EDGE,"E25.7");var subQ1=sQuery(id+"F0.wireOp",EDGE,"E25.1");var subQ2=sQuery(id+"F0.wireOp",EDGE,"E25.6");var subQ3=sQuery(id+"F0.wireOp",EDGE,"E25.5");var subQ4=sQuery(id+"F0.wireOp",EDGE,"E25.4");var subQ5=sQuery(id+"F0.wireOp",EDGE,"E25.0");var subQ6=sQuery(id+"F0.wireOp",EDGE,"E25.2");var subQ7=sQuery(id+"F0.wireOp",EDGE,"E25.3");Q4=makeQuery(id+"F8.boolean.opBoolean","INTERSECT",EDGE,{"derivedFrom":[makeQuery(id+"F5.boolean.opBoolean","SPLIT",FACE,{"disambiguationData":[TD([makeQuery(id+"F2.opExtrude","SWEPT_FACE",FACE,{"disambiguationData":[OSD([subQ5])]})])],"derivedFrom":makeQuery(id+"F3.boolean.opBoolean","COPY",FACE,{"derivedFrom":makeQuery(id+"F3.opExtrude","CAP_FACE",FACE,{"disambiguationData":[OSD([subQ5,subQ1,subQ6,subQ7,subQ4,subQ3,subQ2,subQ0])],"isStart":false})})}),makeQuery(id+"F8.opExtrude","SWEPT_FACE",FACE,{"disambiguationData":[OSD([sQuery(id+"F7.wireOp",EDGE,"E67")])]})]});}
            var Q5;
            Q5=makeQuery(id+"F8.boolean.opBoolean","INTERSECT",EDGE,{"disambiguationData":[OD(0.0)],"derivedFrom":[makeQuery(id+"F5.opExtrude","SWEPT_FACE",FACE,{"disambiguationData":[OSD([sQuery(id+"F4.wireOp",EDGE,"E30")])]}),makeQuery(id+"F8.opExtrude","SWEPT_FACE",FACE,{"disambiguationData":[OSD([sQuery(id+"F7.wireOp",EDGE,"E67")])]})]});
            fillet(context, id + "F14", {"entities" : qUnion([Q0, Q1, Q2, Q3, Q4, Q5]), "radius" : 3 * mm, "tangentPropagation" : true, "allowEdgeOverflow" : false});
        }
        {
            var Q0;
            Q0=makeQuery(id+"F1.opExtrude","CAP_EDGE",EDGE,{"disambiguationData":[OSD([sQuery(id+"F0.wireOp",EDGE,"E1.bottom")])],"isStart":false});
            fillet(context, id + "F15", {"entities" : qUnion([Q0]), "radius" : 2 * mm, "tangentPropagation" : true, "allowEdgeOverflow" : false});
        }
        {
            var Q0;
            {var subQ0=sQuery(id+"F0.wireOp",EDGE,"E21.filletArc");var subQ1=sQuery(id+"F0.wireOp",EDGE,"E7");var subQ2=sQuery(id+"F0.wireOp",EDGE,"E6");var subQ3=sQuery(id+"F0.wireOp",EDGE,"E5");var subQ4=sQuery(id+"F0.wireOp",EDGE,"E4");var subQ5=sQuery(id+"F0.wireOp",EDGE,"E22.filletArc");var subQ6=sQuery(id+"F0.wireOp",EDGE,"E1.bottom");var subQ7=sQuery(id+"F0.wireOp",EDGE,"E1.right");var subQ8=sQuery(id+"F0.wireOp",EDGE,"E1.top");var subQ9=sQuery(id+"F0.wireOp",EDGE,"E1.left");var subQ10=sQuery(id+"F0.wireOp",EDGE,"E23.filletArc");var subQ11=sQuery(id+"F0.wireOp",EDGE,"E24.filletArc");Q0=makeQuery(id+"F2.boolean.opBoolean","SPLIT",FACE,{"disambiguationData":[TD([makeQuery(id+"F1.opExtrude","SWEPT_FACE",FACE,{"disambiguationData":[OSD([subQ6])]})])],"derivedFrom":makeQuery(id+"F1.opExtrude","CAP_FACE",FACE,{"disambiguationData":[OSD([subQ6,subQ8,subQ9,subQ7,subQ4,subQ3,subQ2,subQ1,subQ0,subQ5,subQ10,subQ11])],"isStart":true})});}
            var sketch = newSketch(context, id + "F16", { "sketchPlane" : qUnion([Q0])});
            skLineSegment(sketch, "E79", {"start": v(0, 74.25) * mm, "end": v(0, 104.25) * mm, "construction": true});
            skArc(sketch, "E80", {"start": v(15, 104.25) * mm, "mid": v(0, 119.25) * mm, "end": v(-15, 104.25) * mm});
            skLineSegment(sketch, "E81", {"start": v(15, 104.25) * mm, "end": v(15, 92.25) * mm});
            skLineSegment(sketch, "E82", {"start": v(-15, 104.25) * mm, "end": v(-15, 92.25) * mm});
            skLineSegment(sketch, "E83", {"start": v(-15, 92.25) * mm, "end": v(-33, 74.25) * mm});
            skLineSegment(sketch, "E84", {"start": v(15, 92.25) * mm, "end": v(33, 74.25) * mm});
            skCircle(sketch, "E85", {"center": v(0, 104.25) * mm, "radius": 6 * mm});
            skLineSegment(sketch, "E86", {"start": v(-74.25, 0) * mm, "end": v(74.25, 0) * mm, "construction": true});
            skLineSegment(sketch, "E87.MirrorCS", {"start": v(0, -74.25) * mm, "end": v(0, -104.25) * mm, "construction": true});
            skArc(sketch, "E88.MirrorCS", {"start": v(15, -104.25) * mm, "mid": v(0, -119.25) * mm, "end": v(-15, -104.25) * mm});
            skLineSegment(sketch, "E89.MirrorCS", {"start": v(15, -104.25) * mm, "end": v(15, -92.25) * mm});
            skCircle(sketch, "E90.MirrorC", {"center": v(0, -104.25) * mm, "radius": 6 * mm});
            skLineSegment(sketch, "E91.MirrorCS", {"start": v(-15, -104.25) * mm, "end": v(-15, -92.25) * mm});
            skLineSegment(sketch, "E92.MirrorCS", {"start": v(15, -92.25) * mm, "end": v(33, -74.25) * mm});
            skLineSegment(sketch, "E93.MirrorCS", {"start": v(-15, -92.25) * mm, "end": v(-33, -74.25) * mm});
            skSolve(sketch);
        }
        {
            var Q0;
            Q0=makeQuery(id+"F16.imprint","IMPRINT",FACE,{"disambiguationData":[TD([[makeQuery(id+"F16.imprint","IMPRINT",EDGE,{"derivedFrom":sQuery(id+"F16.wireOp",EDGE,"E80")}),1.0]])]});
            var Q1;
            Q1=makeQuery(id+"F16.imprint","IMPRINT",FACE,{"disambiguationData":[TD([[makeQuery(id+"F16.imprint","IMPRINT",EDGE,{"derivedFrom":makeQuery(id+"F1.opExtrude","CAP_EDGE",EDGE,{"disambiguationData":[OSD([sQuery(id+"F0.wireOp",EDGE,"E1.left")])],"isStart":true})}),-1.0]])]});
            var Q2;
            Q2=makeQuery(id+"F16.imprint","IMPRINT",FACE,{"disambiguationData":[TD([[makeQuery(id+"F16.imprint","IMPRINT",EDGE,{"derivedFrom":sQuery(id+"F16.wireOp",EDGE,"E88.MirrorCS")}),-1.0]])]});
            var Q3;
            Q3=makeQuery(id+"F2.opExtrude","CAP_FACE",FACE,{"disambiguationData":[OSD([sQuery(id+"F0.wireOp",EDGE,"E12"),sQuery(id+"F0.wireOp",EDGE,"E13"),sQuery(id+"F0.wireOp",EDGE,"E14"),sQuery(id+"F0.wireOp",EDGE,"E15"),sQuery(id+"F0.wireOp",EDGE,"E17.filletArc"),sQuery(id+"F0.wireOp",EDGE,"E18.filletArc"),sQuery(id+"F0.wireOp",EDGE,"E19.filletArc"),sQuery(id+"F0.wireOp",EDGE,"E20.filletArc"),sQuery(id+"F0.wireOp",EDGE,"E25.0"),sQuery(id+"F0.wireOp",EDGE,"E25.1"),sQuery(id+"F0.wireOp",EDGE,"E25.2"),sQuery(id+"F0.wireOp",EDGE,"E25.3"),sQuery(id+"F0.wireOp",EDGE,"E25.4"),sQuery(id+"F0.wireOp",EDGE,"E25.5"),sQuery(id+"F0.wireOp",EDGE,"E25.6"),sQuery(id+"F0.wireOp",EDGE,"E25.7")])],"isStart":false});
            extrude(context, id + "F17", {"entities" : qUnion([Q0, Q1, Q2]), "endBound" : BoundingType.UP_TO_SURFACE, "endBoundEntityFace" : qUnion([Q3]), "depth" : 25 * mm});
        }
    });
